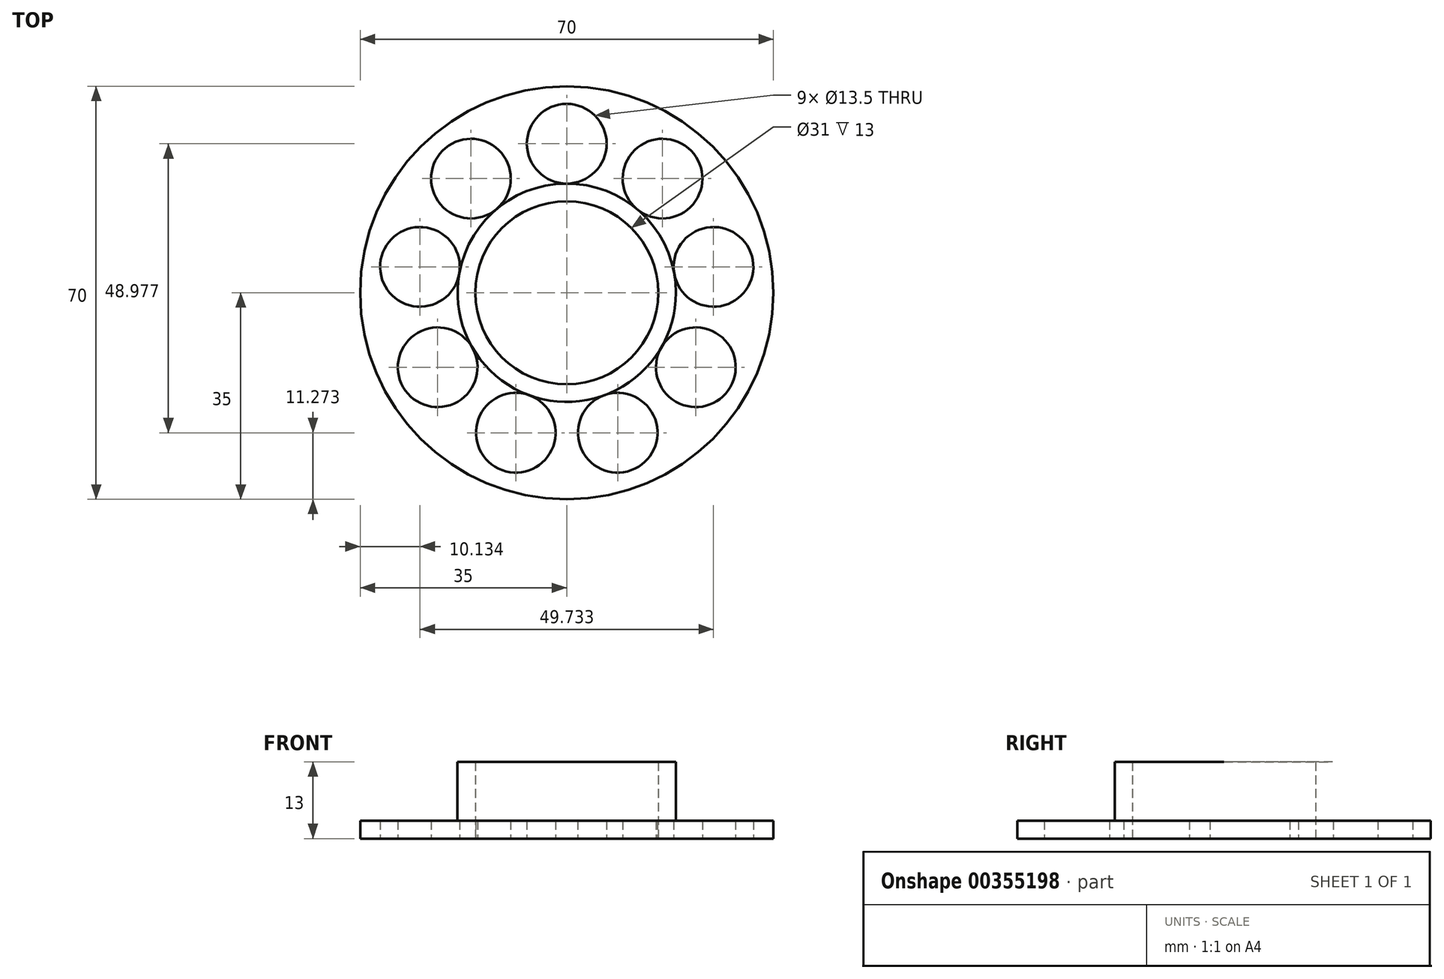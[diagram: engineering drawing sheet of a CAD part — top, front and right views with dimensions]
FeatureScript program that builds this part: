
annotation { "Feature Type Name" : "Feature", "Feature Type Description" : "" }
export const myFeature = defineFeature(function(context is Context, id is Id, definition is map)
    precondition{}
    {
        {
            var Q0;
            Q0=qCreatedBy(makeId("Top.planeOp"),FACE);
            var sketch = newSketch(context, id + "F0", { "sketchPlane" : qUnion([Q0])});
            skCircle(sketch, "E0", {"center": v(0, 0) * mm, "radius": 35 * mm});
            skCircle(sketch, "E1", {"center": v(0, 0) * mm, "radius": 15.5 * mm});
            skCircle(sketch, "E2", {"center": v(0, 25.25) * mm, "radius": 6.75 * mm});
            skPoint(sketch, "E3", {"position": v(0, 35) * mm});
            skPoint(sketch, "E4", {"position": v(0, 15.5) * mm});
            skCircle(sketch, "E5.1.0", {"center": v(-16.23, 19.34) * mm, "radius": 6.75 * mm});
            skCircle(sketch, "E5.2.0", {"center": v(-24.87, 4.38) * mm, "radius": 6.75 * mm});
            skCircle(sketch, "E5.3.0", {"center": v(-21.87, -12.62) * mm, "radius": 6.75 * mm});
            skCircle(sketch, "E5.4.0", {"center": v(-8.64, -23.73) * mm, "radius": 6.75 * mm});
            skCircle(sketch, "E5.5.0", {"center": v(8.64, -23.73) * mm, "radius": 6.75 * mm});
            skCircle(sketch, "E5.6.0", {"center": v(21.87, -12.63) * mm, "radius": 6.75 * mm});
            skCircle(sketch, "E5.7.0", {"center": v(24.87, 4.38) * mm, "radius": 6.75 * mm});
            skCircle(sketch, "E5.8.0", {"center": v(16.23, 19.34) * mm, "radius": 6.75 * mm});
            skCircle(sketch, "E6", {"center": v(0, 0) * mm, "radius": 18.5 * mm});
            skSolve(sketch);
        }
        {
            var Q0;
            Q0=makeQuery(id+"F0.imprint","IMPRINT",FACE,{"disambiguationData":[TD([[makeQuery(id+"F0.imprint","IMPRINT",EDGE,{"derivedFrom":sQuery(id+"F0.wireOp",EDGE,"E0")}),1.0]])]});
            var Q1;
            Q1=makeQuery(id+"F0.imprint","IMPRINT",FACE,{"disambiguationData":[TD([[makeQuery(id+"F0.imprint","IMPRINT",EDGE,{"derivedFrom":sQuery(id+"F0.wireOp",EDGE,"E1")}),-1.0]])]});
            extrude(context, id + "F1", {"entities" : qUnion([Q0, Q1]), "depth" : 3 * mm});
        }
        {
            var Q0;
            Q0=makeQuery(id+"F0.imprint","IMPRINT",FACE,{"disambiguationData":[TD([[makeQuery(id+"F0.imprint","IMPRINT",EDGE,{"derivedFrom":sQuery(id+"F0.wireOp",EDGE,"E1")}),-1.0]])]});
            extrude(context, id + "F2", {"entities" : qUnion([Q0]), "operationType" : NewBodyOperationType.ADD, "depth" : 13 * mm});
        }
    });
